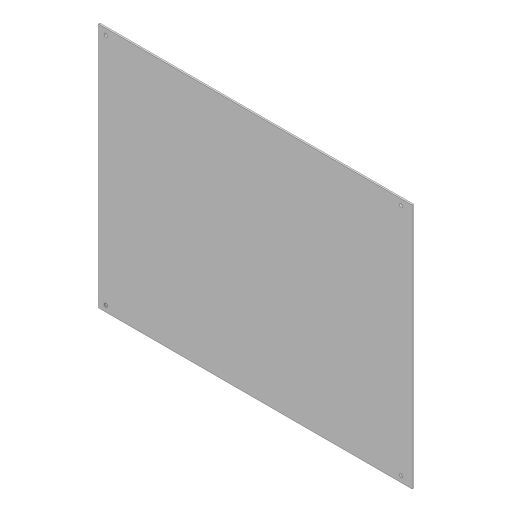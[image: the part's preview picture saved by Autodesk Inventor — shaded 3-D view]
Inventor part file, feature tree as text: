
AUTODESK INVENTOR PART (.ipt)
format: ipt  version: 2023 (Build 270158000, 158)  size: 102,400 bytes
history: native  units: mm
features: sketch x1, extrude x1, hole x1
ambient origin geometry x8: Origin, YZ Plane, XZ Plane, XY Plane, X Axis, Y Axis, Z Axis, Center Point
bodies: Solid1 (feature_tree)
feature tree (3):
  sketch  "Sketch1"  dims[d2=638.0mm d3=500.0mm d10=22.5mm d11=15.5mm d12=12.5mm d13=12.5mm d14=12.5mm d15=12.5mm d16=3.0mm d17=0.0mm d18=6.4mm d19=6.0mm d20=4.0mm d21=2.0mm d22=90.0deg d23=8.0mm d24=20.594885mm]
  extrude  "Extrusion1"  Depth=500.0mm
  hole  "Hole1"  [1 undecoded]
note: 1 required parameter value undecoded (feature->parameter linkage not recoverable at this tier; creation-order binding heuristic only, values carry confidence <= 0.55)
